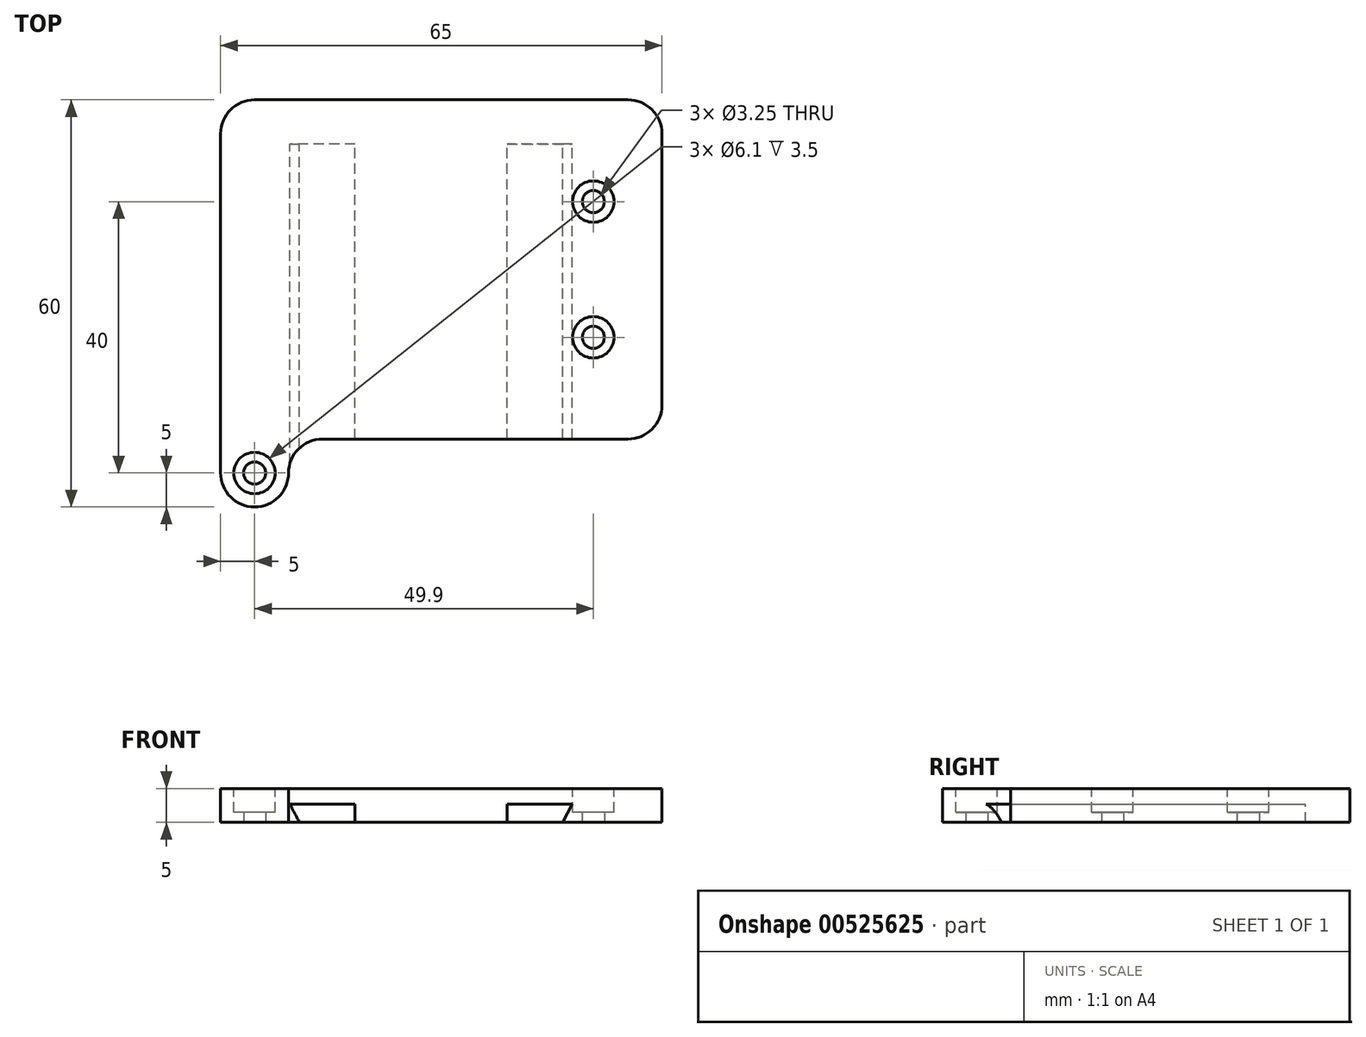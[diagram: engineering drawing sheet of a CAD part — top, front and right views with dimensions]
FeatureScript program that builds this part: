
annotation { "Feature Type Name" : "Feature", "Feature Type Description" : "" }
export const myFeature = defineFeature(function(context is Context, id is Id, definition is map)
    precondition{}
    {
        {
            var Q0;
            Q0=qCreatedBy(makeId("Top.planeOp"),FACE);
            var sketch = newSketch(context, id + "F0", { "sketchPlane" : qUnion([Q0])});
            skLineSegment(sketch, "E0", {"start": v(-32.5, 25) * mm, "end": v(22.5, 25) * mm});
            skLineSegment(sketch, "E1", {"start": v(27.5, 20) * mm, "end": v(27.5, -20) * mm});
            skLineSegment(sketch, "E2", {"start": v(22.5, -25) * mm, "end": v(-22.5, -25) * mm});
            skLineSegment(sketch, "E3", {"start": v(-27.5, -30) * mm, "end": v(-27.5, -30) * mm});
            skLineSegment(sketch, "E4", {"start": v(-32.5, -35) * mm, "end": v(-32.5, -35) * mm});
            skLineSegment(sketch, "E5", {"start": v(-37.5, -30) * mm, "end": v(-37.5, 20) * mm});
            skPoint(sketch, "E6.visualSharp", {"position": v(27.5, 25) * mm});
            skArc(sketch, "E6.filletArc", {"start": v(27.5, 20) * mm, "mid": v(26.04, 23.54) * mm, "end": v(22.5, 25) * mm});
            skPoint(sketch, "E7.visualSharp", {"position": v(27.5, -25) * mm});
            skArc(sketch, "E7.filletArc", {"start": v(22.5, -25) * mm, "mid": v(26.04, -23.54) * mm, "end": v(27.5, -20) * mm});
            skPoint(sketch, "E8.visualSharp", {"position": v(-27.5, -25) * mm});
            skArc(sketch, "E8.filletArc", {"start": v(-22.5, -25) * mm, "mid": v(-26.04, -26.46) * mm, "end": v(-27.5, -30) * mm});
            skPoint(sketch, "E9.visualSharp", {"position": v(-27.5, -35) * mm});
            skArc(sketch, "E9.filletArc", {"start": v(-32.5, -35) * mm, "mid": v(-28.96, -33.54) * mm, "end": v(-27.5, -30) * mm});
            skPoint(sketch, "E10.visualSharp", {"position": v(-37.5, -35) * mm});
            skArc(sketch, "E10.filletArc", {"start": v(-37.5, -30) * mm, "mid": v(-36.04, -33.54) * mm, "end": v(-32.5, -35) * mm});
            skCircle(sketch, "E11", {"center": v(-32.5, -30) * mm, "radius": 1.63 * mm});
            skCircle(sketch, "E12", {"center": v(17.4, 10) * mm, "radius": 1.63 * mm});
            skCircle(sketch, "E13", {"center": v(17.4, -10) * mm, "radius": 1.63 * mm});
            skPoint(sketch, "E14.visualSharp", {"position": v(-37.5, 25) * mm});
            skArc(sketch, "E14.filletArc", {"start": v(-32.5, 25) * mm, "mid": v(-36.04, 23.54) * mm, "end": v(-37.5, 20) * mm});
            skSolve(sketch);
        }
        {
            var Q0;
            Q0=makeQuery(id+"F0.imprint","IMPRINT",FACE,{"disambiguationData":[TD([[makeQuery(id+"F0.imprint","IMPRINT",EDGE,{"derivedFrom":sQuery(id+"F0.wireOp",EDGE,"E0")}),-1.0]])]});
            extrude(context, id + "F1", {"entities" : qUnion([Q0]), "depth" : 5 * mm});
        }
        {
            var Q0;
            Q0=makeQuery(id+"F1.opExtrude","CAP_FACE",FACE,{"disambiguationData":[OSD([sQuery(id+"F0.wireOp",EDGE,"E0"),sQuery(id+"F0.wireOp",EDGE,"E1"),sQuery(id+"F0.wireOp",EDGE,"E2"),sQuery(id+"F0.wireOp",EDGE,"E5"),sQuery(id+"F0.wireOp",EDGE,"E6.filletArc"),sQuery(id+"F0.wireOp",EDGE,"E7.filletArc"),sQuery(id+"F0.wireOp",EDGE,"E8.filletArc"),sQuery(id+"F0.wireOp",EDGE,"E9.filletArc"),sQuery(id+"F0.wireOp",EDGE,"E10.filletArc"),sQuery(id+"F0.wireOp",EDGE,"nNRTAZ3m-UcFT-XEbX-bW4l-1CdXOK1OszjN"),sQuery(id+"F0.wireOp",EDGE,"OskZh1Qr-N4c8-G8Yp-psBz-cHskyBAqI7m4"),sQuery(id+"F0.wireOp",EDGE,"E11")])],"isStart":false});
            var sketch = newSketch(context, id + "F2", { "sketchPlane" : qUnion([Q0])});
            skCircle(sketch, "E15", {"center": v(-32.5, -30) * mm, "radius": 3.05 * mm});
            skCircle(sketch, "E16", {"center": v(17.4, 10) * mm, "radius": 3.05 * mm});
            skCircle(sketch, "E17", {"center": v(17.4, -10) * mm, "radius": 3.05 * mm});
            skSolve(sketch);
        }
        {
            var Q0;
            Q0=makeQuery(id+"F2.imprint","IMPRINT",FACE,{"disambiguationData":[TD([[makeQuery(id+"F2.imprint","IMPRINT",EDGE,{"derivedFrom":sQuery(id+"F2.wireOp",EDGE,"E16")}),1.0]])]});
            var Q1;
            Q1=makeQuery(id+"F2.imprint","IMPRINT",FACE,{"disambiguationData":[TD([[makeQuery(id+"F2.imprint","IMPRINT",EDGE,{"derivedFrom":sQuery(id+"F2.wireOp",EDGE,"E17")}),1.0]])]});
            var Q2;
            Q2=makeQuery(id+"F2.imprint","IMPRINT",FACE,{"disambiguationData":[TD([[makeQuery(id+"F2.imprint","IMPRINT",EDGE,{"derivedFrom":sQuery(id+"F2.wireOp",EDGE,"E15")}),1.0]])]});
            extrude(context, id + "F3", {"entities" : qUnion([Q0, Q1, Q2]), "operationType" : NewBodyOperationType.REMOVE, "oppositeDirection" : true, "depth" : 3.5 * mm});
        }
        {
            var Q0;
            Q0=makeQuery(id+"F1.opExtrude","SWEPT_FACE",FACE,{"disambiguationData":[OSD([sQuery(id+"F0.wireOp",EDGE,"E2")])]});
            var sketch = newSketch(context, id + "F4", { "sketchPlane" : qUnion([Q0])});
            skLineSegment(sketch, "E18", {"start": v(4.7, 0) * mm, "end": v(4.7, 2.7) * mm});
            skLineSegment(sketch, "E19", {"start": v(4.7, 2.7) * mm, "end": v(14.29, 2.7) * mm});
            skLineSegment(sketch, "E20", {"start": v(14.29, 2.71) * mm, "end": v(12.88, 0) * mm});
            skLineSegment(sketch, "E21", {"start": v(12.88, 0) * mm, "end": v(4.7, 0) * mm});
            skLineSegment(sketch, "E22", {"start": v(-17.71, 0) * mm, "end": v(-17.71, 2.71) * mm});
            skLineSegment(sketch, "E23", {"start": v(-17.71, 2.71) * mm, "end": v(-27.3, 2.7) * mm});
            skLineSegment(sketch, "E24", {"start": v(-27.3, 2.71) * mm, "end": v(-25.9, 0) * mm});
            skLineSegment(sketch, "E25", {"start": v(-25.9, 0) * mm, "end": v(-17.71, 0) * mm});
            skSolve(sketch);
        }
        {
            var Q0;
            {var subQ0=sQuery(id+"F4.wireOp",EDGE,"E22");Q0=makeQuery(id+"F4.imprint","IMPRINT",FACE,{"disambiguationData":[TD([[makeQuery(id+"F4.imprint","IMPRINT",EDGE,{"derivedFrom":subQ0}),1.0]])]});}
            var Q1;
            Q1=makeQuery(id+"F4.imprint","IMPRINT",FACE,{"disambiguationData":[TD([[makeQuery(id+"F4.imprint","IMPRINT",EDGE,{"derivedFrom":sQuery(id+"F4.wireOp",EDGE,"E18")}),-1.0]])]});
            var Q2;
            {var subQ0=sQuery(id+"F4.wireOp",EDGE,"E24");Q2=makeQuery(id+"F4.imprint","IMPRINT",FACE,{"disambiguationData":[TD([[makeQuery(id+"F4.imprint","IMPRINT",EDGE,{"derivedFrom":subQ0}),1.0]])]});}
            extrude(context, id + "F5", {"entities" : qUnion([Q0, Q1, Q2]), "operationType" : NewBodyOperationType.REMOVE, "endBound" : BoundingType.SYMMETRIC, "depth" : 86.9 * mm});
        }
    });
